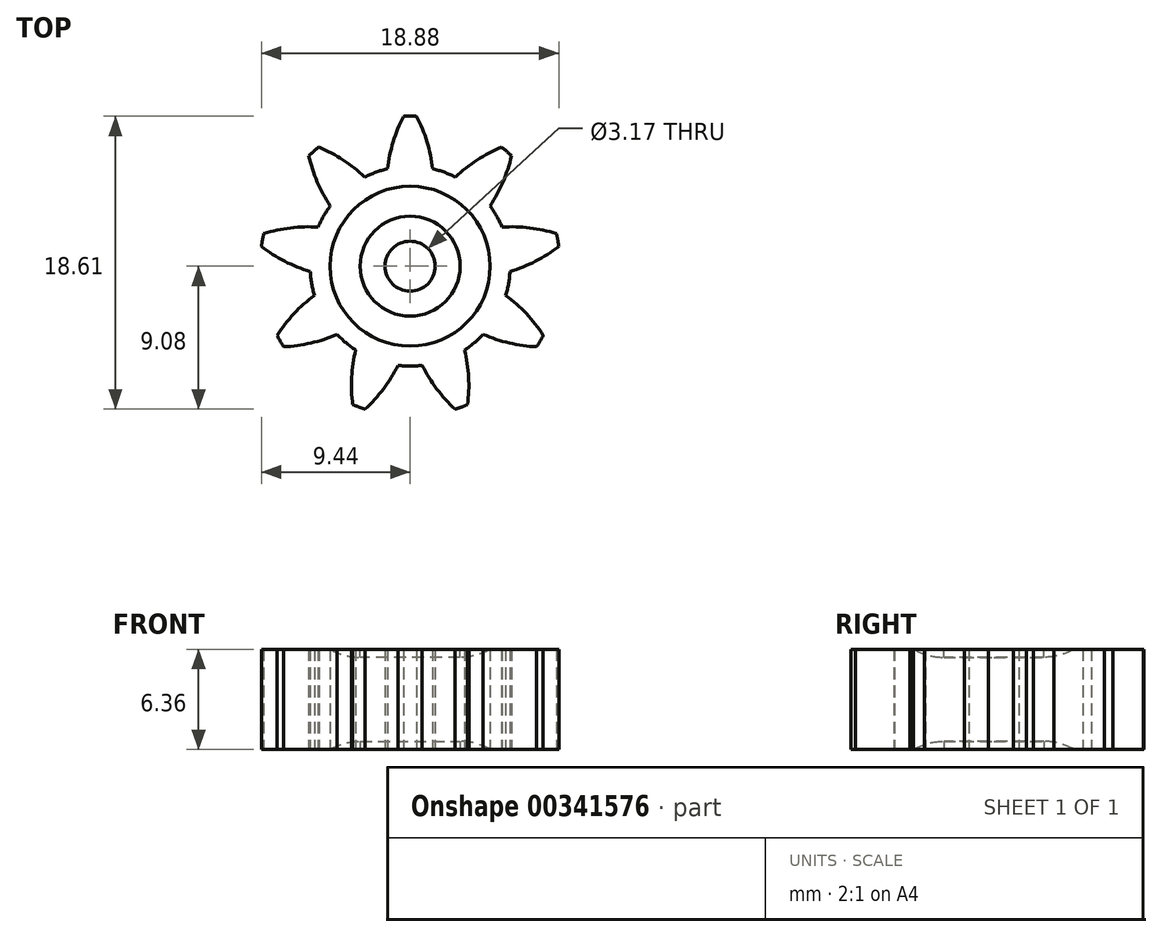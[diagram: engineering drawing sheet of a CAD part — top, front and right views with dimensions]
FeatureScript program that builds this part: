
annotation { "Feature Type Name" : "Feature", "Feature Type Description" : "" }
export const myFeature = defineFeature(function(context is Context, id is Id, definition is map)
    precondition{}
    {
        {
            var Q0;
            Q0=qCreatedBy(makeId("Top.planeOp"),FACE);
            var sketch = newSketch(context, id + "F0", { "sketchPlane" : qUnion([Q0])});
            skCircle(sketch, "E0", {"center": v(0, 0) * mm, "radius": 6.35 * mm});
            skCircle(sketch, "E1", {"center": v(0, 0) * mm, "radius": 1.59 * mm});
            skCircle(sketch, "E2", {"center": v(0, 0) * mm, "radius": 9.53 * mm, "construction": true});
            skLineSegment(sketch, "E3", {"start": v(0, 0) * mm, "end": v(-7.84, 5) * mm, "construction": true});
            skLineSegment(sketch, "E4", {"start": v(0, 0) * mm, "end": v(8.03, 5.12) * mm, "construction": true});
            skArc(sketch, "E5", {"start": v(1.43, 6.19) * mm, "mid": v(1.08, 7.9) * mm, "end": v(0.42, 9.52) * mm});
            skArc(sketch, "E6", {"start": v(-1.43, 6.19) * mm, "mid": v(-1.08, 7.9) * mm, "end": v(-0.42, 9.52) * mm});
            skArc(sketch, "E7", {"start": v(-0.42, 9.52) * mm, "mid": v(0.06, 9.52) * mm, "end": v(0.53, 9.51) * mm});
            skArc(sketch, "E8.1.0", {"start": v(-2.88, 5.66) * mm, "mid": v(-4.25, 6.74) * mm, "end": v(-5.8, 7.56) * mm});
            skArc(sketch, "E8.1.1", {"start": v(-6.43, 7.02) * mm, "mid": v(-6.08, 7.33) * mm, "end": v(-5.71, 7.62) * mm});
            skArc(sketch, "E8.1.2", {"start": v(-5.07, 3.82) * mm, "mid": v(-5.9, 5.36) * mm, "end": v(-6.43, 7.02) * mm});
            skArc(sketch, "E8.2.0", {"start": v(-5.84, 2.48) * mm, "mid": v(-7.6, 2.43) * mm, "end": v(-9.3, 2.06) * mm});
            skArc(sketch, "E8.2.1", {"start": v(-9.44, 1.24) * mm, "mid": v(-9.37, 1.7) * mm, "end": v(-9.27, 2.17) * mm});
            skArc(sketch, "E8.2.2", {"start": v(-6.34, -0.34) * mm, "mid": v(-7.97, 0.31) * mm, "end": v(-9.44, 1.24) * mm});
            skArc(sketch, "E8.3.0", {"start": v(-6.07, -1.85) * mm, "mid": v(-7.38, -3.02) * mm, "end": v(-8.45, -4.4) * mm});
            skArc(sketch, "E8.3.1", {"start": v(-8.03, -5.12) * mm, "mid": v(-8.28, -4.71) * mm, "end": v(-8.5, -4.3) * mm});
            skArc(sketch, "E8.3.2", {"start": v(-4.64, -4.33) * mm, "mid": v(-6.3, -4.88) * mm, "end": v(-8.03, -5.12) * mm});
            skArc(sketch, "E8.4.0", {"start": v(-3.46, -5.32) * mm, "mid": v(-3.71, -7.05) * mm, "end": v(-3.65, -8.8) * mm});
            skArc(sketch, "E8.4.1", {"start": v(-2.86, -9.08) * mm, "mid": v(-3.3, -8.93) * mm, "end": v(-3.75, -8.76) * mm});
            skArc(sketch, "E8.4.2", {"start": v(-0.77, -6.3) * mm, "mid": v(-1.69, -7.8) * mm, "end": v(-2.86, -9.08) * mm});
            skArc(sketch, "E8.5.0", {"start": v(0.77, -6.3) * mm, "mid": v(1.69, -7.8) * mm, "end": v(2.86, -9.08) * mm});
            skArc(sketch, "E8.5.1", {"start": v(3.65, -8.8) * mm, "mid": v(3.2, -8.97) * mm, "end": v(2.76, -9.12) * mm});
            skArc(sketch, "E8.5.2", {"start": v(3.46, -5.32) * mm, "mid": v(3.71, -7.05) * mm, "end": v(3.65, -8.8) * mm});
            skArc(sketch, "E8.6.0", {"start": v(4.64, -4.33) * mm, "mid": v(6.3, -4.88) * mm, "end": v(8.03, -5.12) * mm});
            skArc(sketch, "E8.6.1", {"start": v(8.45, -4.4) * mm, "mid": v(8.22, -4.81) * mm, "end": v(7.97, -5.21) * mm});
            skArc(sketch, "E8.6.2", {"start": v(6.07, -1.85) * mm, "mid": v(7.38, -3.02) * mm, "end": v(8.45, -4.4) * mm});
            skArc(sketch, "E8.7.0", {"start": v(6.34, -0.34) * mm, "mid": v(7.97, 0.31) * mm, "end": v(9.44, 1.24) * mm});
            skArc(sketch, "E8.7.1", {"start": v(9.3, 2.06) * mm, "mid": v(9.39, 1.6) * mm, "end": v(9.46, 1.13) * mm});
            skArc(sketch, "E8.7.2", {"start": v(5.84, 2.48) * mm, "mid": v(7.6, 2.43) * mm, "end": v(9.3, 2.06) * mm});
            skCircle(sketch, "E9", {"center": v(0, 0) * mm, "radius": 3.18 * mm});
            skCircle(sketch, "E10", {"center": v(0, 0) * mm, "radius": 4.76 * mm});
            skCircle(sketch, "E11", {"center": v(-8.03, 5.12) * mm, "radius": 9.53 * mm, "construction": true});
            skCircle(sketch, "E12", {"center": v(8.03, 5.12) * mm, "radius": 9.53 * mm, "construction": true});
            skArc(sketch, "E13.1.8.0", {"start": v(5.07, 3.82) * mm, "mid": v(5.9, 5.36) * mm, "end": v(6.43, 7.02) * mm});
            skArc(sketch, "E13.4.8.0", {"start": v(5.8, 7.56) * mm, "mid": v(6.16, 7.26) * mm, "end": v(6.52, 6.95) * mm});
            skArc(sketch, "E13.8.8.0", {"start": v(2.88, 5.66) * mm, "mid": v(4.25, 6.74) * mm, "end": v(5.8, 7.56) * mm});
            skSolve(sketch);
        }
        {
            var Q0;
            Q0 = qSketchRegion(id + "F0", true);
            var Q1;
            Q1=makeQuery(id+"F0.imprint","IMPRINT",FACE,{"disambiguationData":[TD([[makeQuery(id+"F0.imprint","IMPRINT",EDGE,{"derivedFrom":sQuery(id+"F0.wireOp",EDGE,"E1")}),-1.0]])]});
            var Q2;
            Q2=makeQuery(id+"F0.imprint","IMPRINT",FACE,{"disambiguationData":[TD([[makeQuery(id+"F0.imprint","IMPRINT",EDGE,{"derivedFrom":sQuery(id+"F0.wireOp",EDGE,"E9")}),-1.0]])]});
            extrude(context, id + "F1", {"entities" : qUnion([Q0, Q1, Q2]), "endBound" : BoundingType.SYMMETRIC, "depth" : 6.35 * mm});
        }
        {
            var Q0;
            Q0=makeQuery(id+"F1.opExtrude","CAP_FACE",FACE,{"disambiguationData":[OSD([sQuery(id+"F0.wireOp",EDGE,"E0"),sQuery(id+"F0.wireOp",EDGE,"E1"),sQuery(id+"F0.wireOp",EDGE,"E5"),sQuery(id+"F0.wireOp",EDGE,"E6"),sQuery(id+"F0.wireOp",EDGE,"E7"),sQuery(id+"F0.wireOp",EDGE,"E8.1.0"),sQuery(id+"F0.wireOp",EDGE,"E8.1.1"),sQuery(id+"F0.wireOp",EDGE,"E8.1.2"),sQuery(id+"F0.wireOp",EDGE,"E8.2.0"),sQuery(id+"F0.wireOp",EDGE,"E8.2.1"),sQuery(id+"F0.wireOp",EDGE,"E8.2.2"),sQuery(id+"F0.wireOp",EDGE,"E8.3.0"),sQuery(id+"F0.wireOp",EDGE,"E8.3.1"),sQuery(id+"F0.wireOp",EDGE,"E8.3.2"),sQuery(id+"F0.wireOp",EDGE,"E8.4.0"),sQuery(id+"F0.wireOp",EDGE,"E8.4.1"),sQuery(id+"F0.wireOp",EDGE,"E8.4.2"),sQuery(id+"F0.wireOp",EDGE,"E8.5.0"),sQuery(id+"F0.wireOp",EDGE,"E8.5.1"),sQuery(id+"F0.wireOp",EDGE,"E8.5.2"),sQuery(id+"F0.wireOp",EDGE,"E8.6.0"),sQuery(id+"F0.wireOp",EDGE,"E8.6.1"),sQuery(id+"F0.wireOp",EDGE,"E8.6.2"),sQuery(id+"F0.wireOp",EDGE,"E8.7.0"),sQuery(id+"F0.wireOp",EDGE,"E8.7.1"),sQuery(id+"F0.wireOp",EDGE,"E8.7.2"),sQuery(id+"F0.wireOp",EDGE,"E13.1.8.0"),sQuery(id+"F0.wireOp",EDGE,"E13.4.8.0"),sQuery(id+"F0.wireOp",EDGE,"E13.8.8.0")])],"isStart":true});
            var sketch = newSketch(context, id + "F2", { "sketchPlane" : qUnion([Q0])});
            skCircle(sketch, "E14", {"center": v(0, 0) * mm, "radius": 5.08 * mm});
            skCircle(sketch, "E15", {"center": v(0, 0) * mm, "radius": 3.18 * mm});
            skSolve(sketch);
        }
        {
            var Q0;
            Q0 = qSketchRegion(id + "F2", true);
            extrude(context, id + "F3", {"entities" : qUnion([Q0]), "operationType" : NewBodyOperationType.REMOVE, "oppositeDirection" : true, "depth" : 0.5 * mm});
        }
        {
            var Q0;
            Q0=makeQuery(id+"F1.opExtrude","CAP_FACE",FACE,{"disambiguationData":[OSD([sQuery(id+"F0.wireOp",EDGE,"E0"),sQuery(id+"F0.wireOp",EDGE,"E1"),sQuery(id+"F0.wireOp",EDGE,"E5"),sQuery(id+"F0.wireOp",EDGE,"E6"),sQuery(id+"F0.wireOp",EDGE,"E7"),sQuery(id+"F0.wireOp",EDGE,"E8.1.0"),sQuery(id+"F0.wireOp",EDGE,"E8.1.1"),sQuery(id+"F0.wireOp",EDGE,"E8.1.2"),sQuery(id+"F0.wireOp",EDGE,"E8.2.0"),sQuery(id+"F0.wireOp",EDGE,"E8.2.1"),sQuery(id+"F0.wireOp",EDGE,"E8.2.2"),sQuery(id+"F0.wireOp",EDGE,"E8.3.0"),sQuery(id+"F0.wireOp",EDGE,"E8.3.1"),sQuery(id+"F0.wireOp",EDGE,"E8.3.2"),sQuery(id+"F0.wireOp",EDGE,"E8.4.0"),sQuery(id+"F0.wireOp",EDGE,"E8.4.1"),sQuery(id+"F0.wireOp",EDGE,"E8.4.2"),sQuery(id+"F0.wireOp",EDGE,"E8.5.0"),sQuery(id+"F0.wireOp",EDGE,"E8.5.1"),sQuery(id+"F0.wireOp",EDGE,"E8.5.2"),sQuery(id+"F0.wireOp",EDGE,"E8.6.0"),sQuery(id+"F0.wireOp",EDGE,"E8.6.1"),sQuery(id+"F0.wireOp",EDGE,"E8.6.2"),sQuery(id+"F0.wireOp",EDGE,"E8.7.0"),sQuery(id+"F0.wireOp",EDGE,"E8.7.1"),sQuery(id+"F0.wireOp",EDGE,"E8.7.2"),sQuery(id+"F0.wireOp",EDGE,"E13.1.8.0"),sQuery(id+"F0.wireOp",EDGE,"E13.4.8.0"),sQuery(id+"F0.wireOp",EDGE,"E13.8.8.0")])],"isStart":false});
            var sketch = newSketch(context, id + "F4", { "sketchPlane" : qUnion([Q0])});
            skCircle(sketch, "E16", {"center": v(0, 0) * mm, "radius": 5.08 * mm});
            skCircle(sketch, "E17", {"center": v(0, 0) * mm, "radius": 3.18 * mm});
            skSolve(sketch);
        }
        {
            var Q0;
            Q0 = qSketchRegion(id + "F4", true);
            extrude(context, id + "F5", {"entities" : qUnion([Q0]), "operationType" : NewBodyOperationType.REMOVE, "oppositeDirection" : true, "depth" : 0.5 * mm});
        }
        {
            var Q0;
            Q0=makeQuery(id+"F5.boolean.opBoolean","COPY",EDGE,{"derivedFrom":makeQuery(id+"F5.opExtrude","CAP_EDGE",EDGE,{"disambiguationData":[OSD([sQuery(id+"F4.wireOp",EDGE,"E16")])],"isStart":false})});
            var Q1;
            Q1=makeQuery(id+"F3.boolean.opBoolean","COPY",EDGE,{"derivedFrom":makeQuery(id+"F3.opExtrude","CAP_EDGE",EDGE,{"disambiguationData":[OSD([sQuery(id+"F2.wireOp",EDGE,"E14")])],"isStart":false})});
            fillet(context, id + "F6", {"entities" : qUnion([Q0, Q1]), "radius" : 3.8 * mm, "tangentPropagation" : true, "allowEdgeOverflow" : false});
        }
    });
